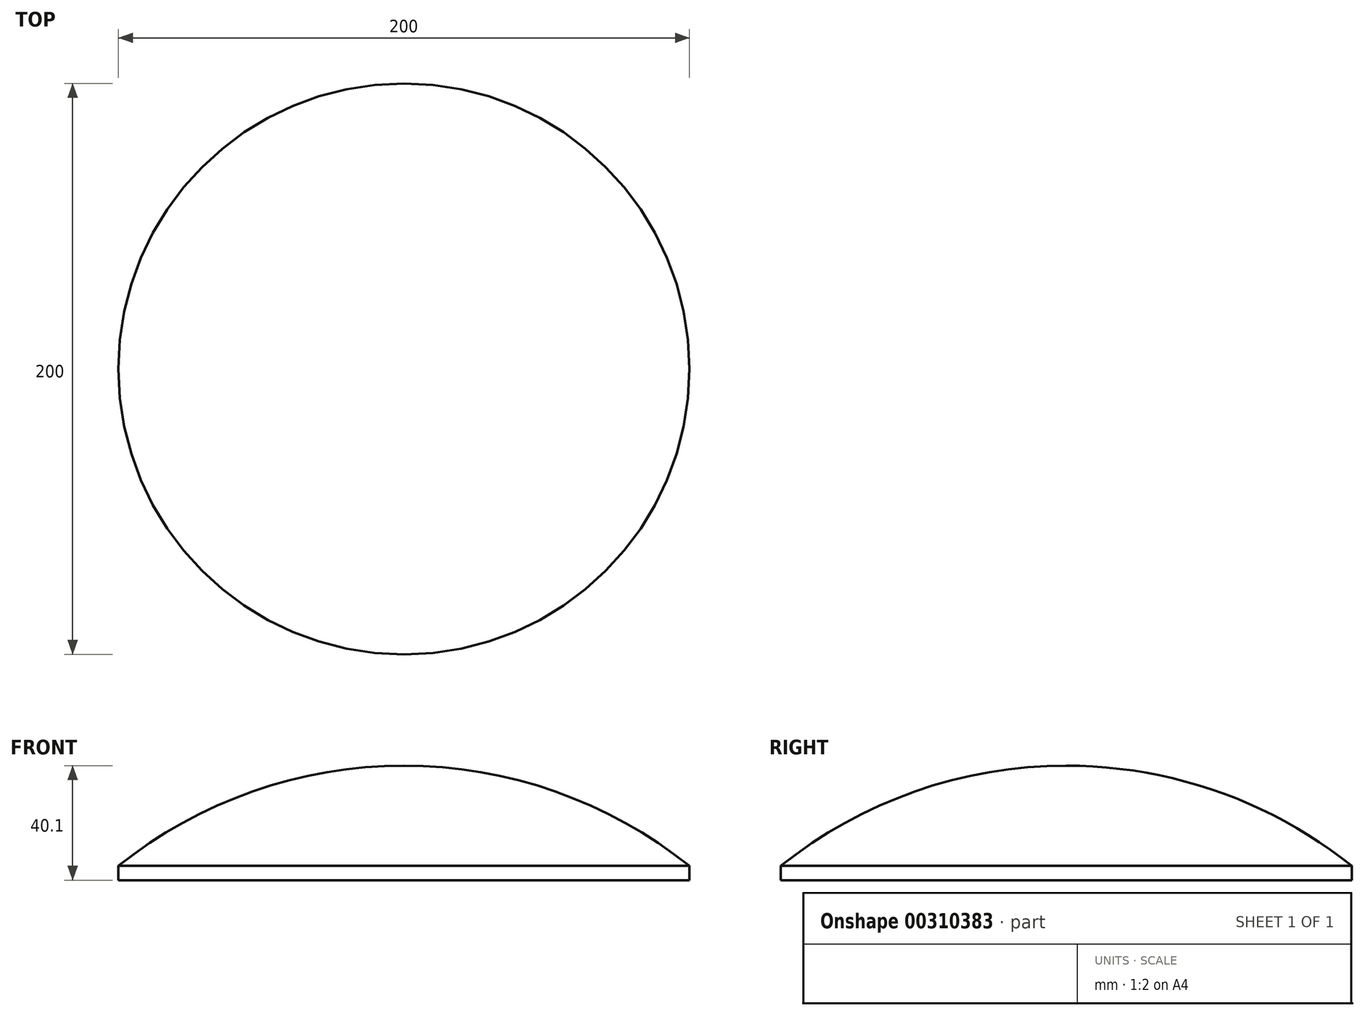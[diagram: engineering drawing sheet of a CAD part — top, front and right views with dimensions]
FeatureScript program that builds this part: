
annotation { "Feature Type Name" : "Feature", "Feature Type Description" : "" }
export const myFeature = defineFeature(function(context is Context, id is Id, definition is map)
    precondition{}
    {
        {
            var Q0;
            Q0=qCreatedBy(makeId("Right.planeOp"),FACE);
            var sketch = newSketch(context, id + "F0", { "sketchPlane" : qUnion([Q0])});
            skArc(sketch, "E0", {"start": v(100, 5) * mm, "mid": v(0, 40.1) * mm, "end": v(-100, 5) * mm});
            skLineSegment(sketch, "E1", {"start": v(-100, 0) * mm, "end": v(100, 0) * mm});
            skLineSegment(sketch, "E2", {"start": v(100, 5) * mm, "end": v(100, 0) * mm});
            skLineSegment(sketch, "E3", {"start": v(-100, 0) * mm, "end": v(-100, 5) * mm});
            skLineSegment(sketch, "E4", {"start": v(0, 0) * mm, "end": v(0, 40.1) * mm});
            skSolve(sketch);
        }
        {
            var Q0;
            {var subQ0=sQuery(id+"F0.wireOp",EDGE,"E2");Q0=makeQuery(id+"F0.imprint","IMPRINT",FACE,{"disambiguationData":[TD([[makeQuery(id+"F0.imprint","IMPRINT",EDGE,{"derivedFrom":subQ0}),-1.0]])]});}
            var Q1;
            Q1=sQuery(id+"F0.wireOp",EDGE,"E4");
            revolve(context, id + "F1", {"entities" : qUnion([Q0]), "axis" : qUnion([Q1]), "revolveType" : RevolveType.FULL});
        }
    });
